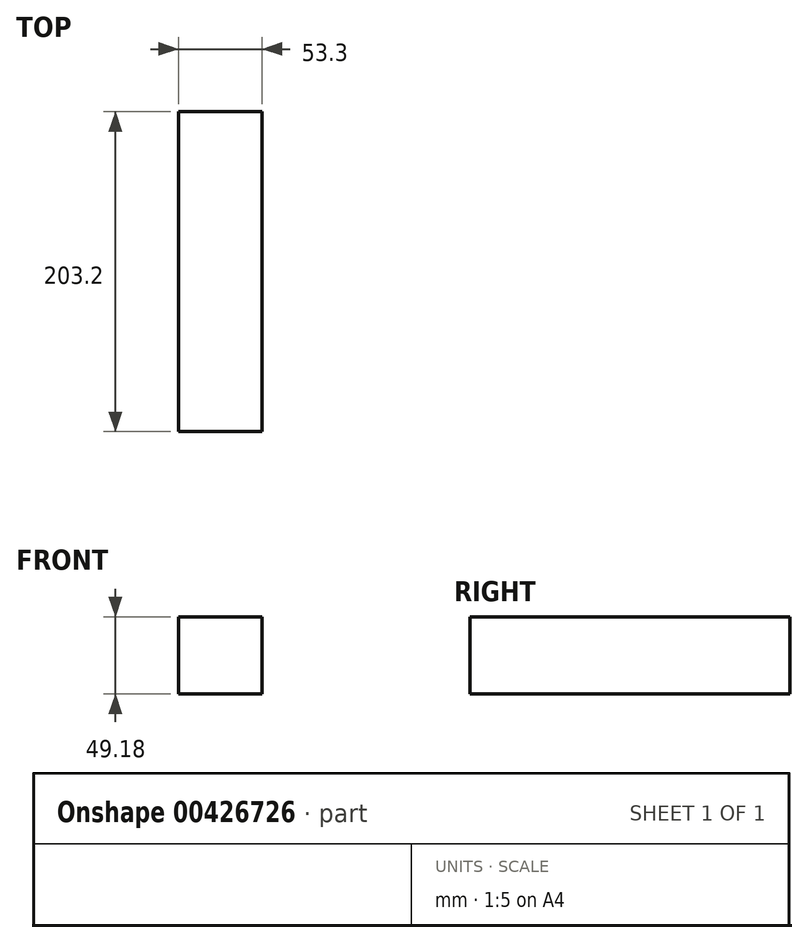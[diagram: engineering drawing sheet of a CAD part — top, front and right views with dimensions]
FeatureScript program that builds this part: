
annotation { "Feature Type Name" : "Feature", "Feature Type Description" : "" }
export const myFeature = defineFeature(function(context is Context, id is Id, definition is map)
    precondition{}
    {
        {
            var Q0;
            Q0=qCreatedBy(makeId("Front.planeOp"),FACE);
            var sketch = newSketch(context, id + "F0", { "sketchPlane" : qUnion([Q0])});
            skPoint(sketch, "E0.0", {"position": v(0, 0) * mm});
            skLineSegment(sketch, "E1.bottom", {"start": v(-26.65, -24.6) * mm, "end": v(26.65, -24.6) * mm});
            skLineSegment(sketch, "E1.top", {"start": v(-26.65, 24.6) * mm, "end": v(26.65, 24.6) * mm});
            skLineSegment(sketch, "E1.left", {"start": v(-26.65, -24.6) * mm, "end": v(-26.65, 24.6) * mm});
            skLineSegment(sketch, "E1.right", {"start": v(26.65, -24.6) * mm, "end": v(26.65, 24.6) * mm});
            skSolve(sketch);
        }
        {
            var Q0;
            Q0=makeQuery(id+"F0.imprint","IMPRINT",FACE,{"disambiguationData":[TD([[makeQuery(id+"F0.imprint","IMPRINT",EDGE,{"derivedFrom":sQuery(id+"F0.wireOp",EDGE,"E1.bottom")}),1.0]])]});
            extrude(context, id + "F1", {"entities" : qUnion([Q0]), "depth" : 203.2 * mm});
        }
    });
